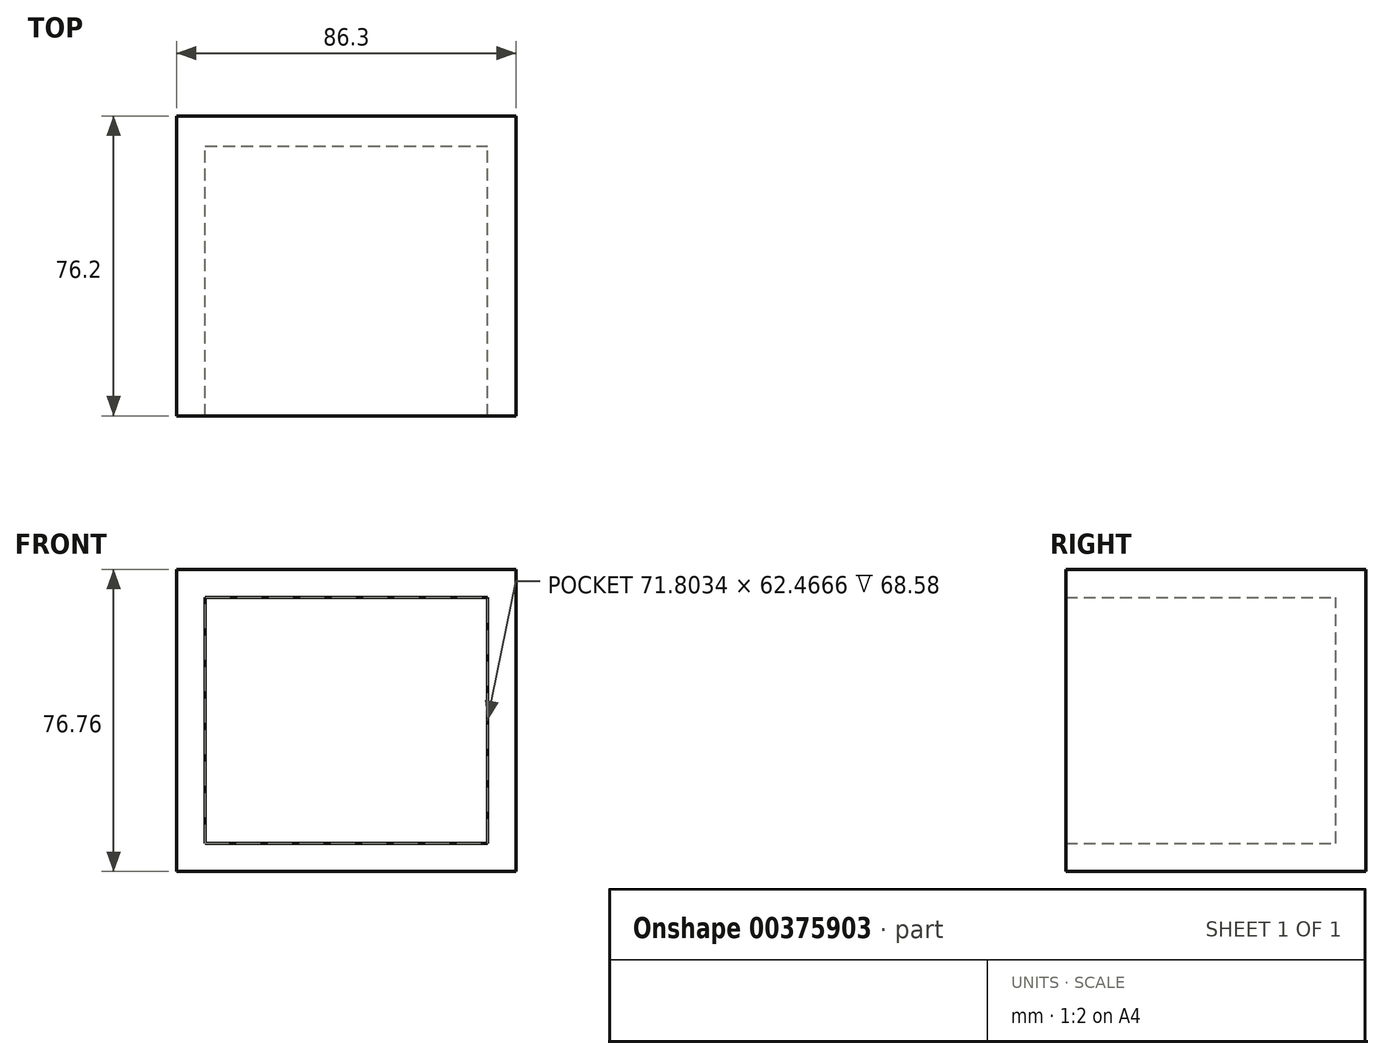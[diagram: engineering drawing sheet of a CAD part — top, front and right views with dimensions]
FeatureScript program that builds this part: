
annotation { "Feature Type Name" : "Feature", "Feature Type Description" : "" }
export const myFeature = defineFeature(function(context is Context, id is Id, definition is map)
    precondition{}
    {
        {
            var Q0;
            Q0=qCreatedBy(makeId("Front.planeOp"),FACE);
            var sketch = newSketch(context, id + "F0", { "sketchPlane" : qUnion([Q0])});
            skLineSegment(sketch, "E0.bottom", {"start": v(43.15, 38.38) * mm, "end": v(-43.15, 38.38) * mm});
            skLineSegment(sketch, "E0.top", {"start": v(43.15, -38.38) * mm, "end": v(-43.15, -38.38) * mm});
            skLineSegment(sketch, "E0.left", {"start": v(43.15, 38.38) * mm, "end": v(43.15, -38.38) * mm});
            skLineSegment(sketch, "E0.right", {"start": v(-43.15, 38.38) * mm, "end": v(-43.15, -38.38) * mm});
            skPoint(sketch, "E0.middle", {"position": v(0, 0) * mm});
            skLineSegment(sketch, "E1.bottom", {"start": v(-35.9, -31.23) * mm, "end": v(35.9, -31.23) * mm});
            skLineSegment(sketch, "E1.top", {"start": v(-35.9, 31.23) * mm, "end": v(35.9, 31.23) * mm});
            skLineSegment(sketch, "E1.left", {"start": v(-35.9, -31.23) * mm, "end": v(-35.9, 31.23) * mm});
            skLineSegment(sketch, "E1.right", {"start": v(35.9, -31.23) * mm, "end": v(35.9, 31.23) * mm});
            skSolve(sketch);
        }
        {
            var Q0;
            Q0=makeQuery(id+"F0.imprint","IMPRINT",FACE,{"disambiguationData":[TD([[makeQuery(id+"F0.imprint","IMPRINT",EDGE,{"derivedFrom":sQuery(id+"F0.wireOp",EDGE,"E1.bottom")}),1.0]])]});
            extrude(context, id + "F1", {"entities" : qUnion([Q0]), "depth" : 7.62 * mm});
        }
        {
            var Q0;
            Q0 = qSketchRegion(id + "F0", true);
            extrude(context, id + "F2", {"entities" : qUnion([Q0]), "operationType" : NewBodyOperationType.ADD, "depth" : 76.2 * mm});
        }
    });
